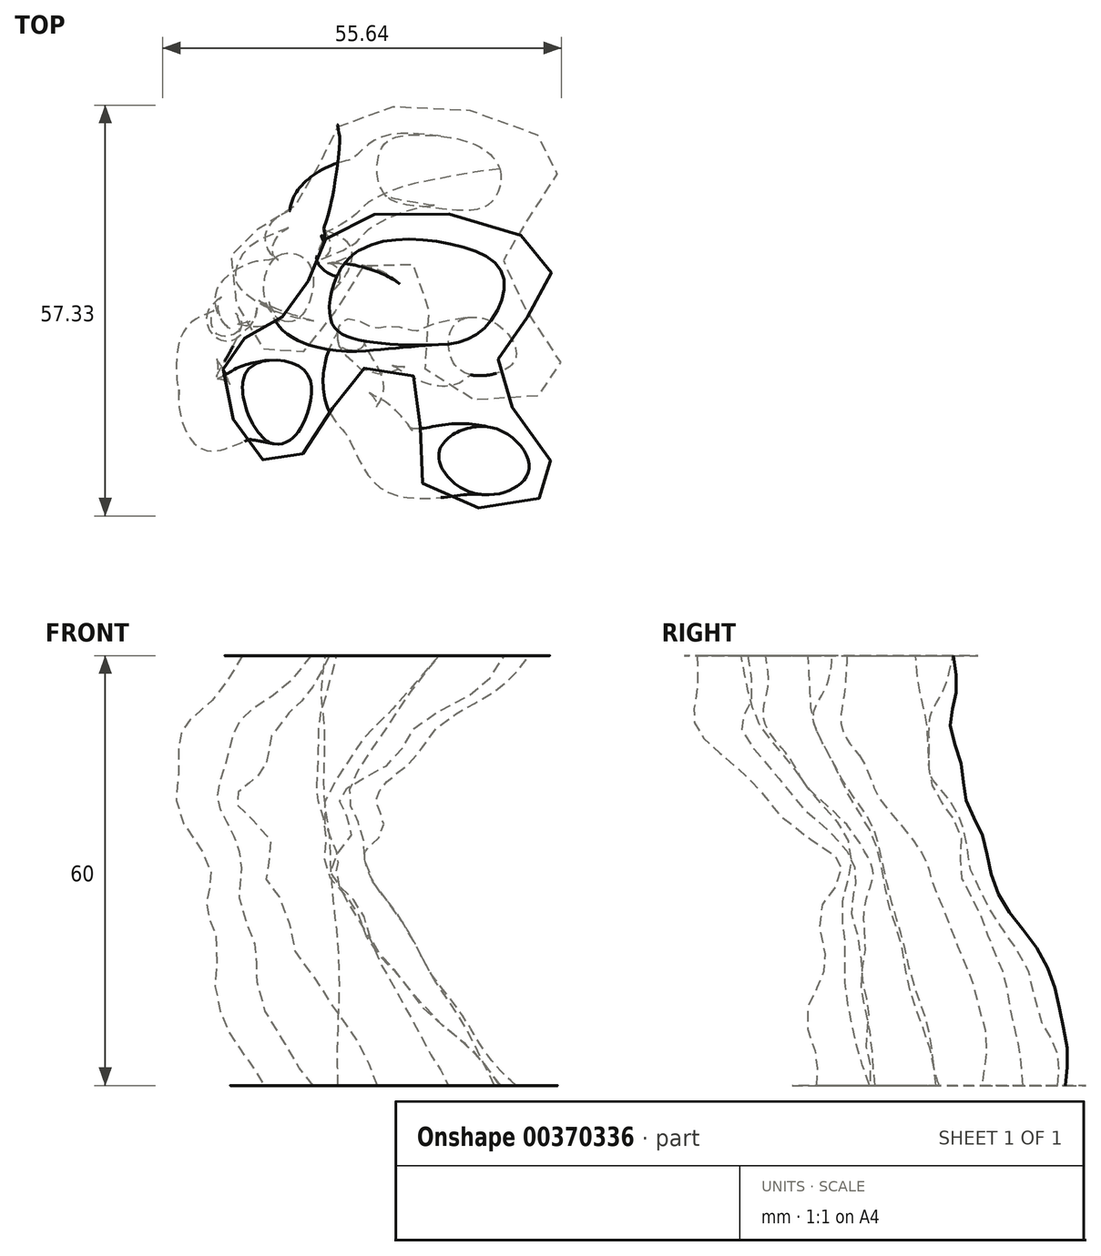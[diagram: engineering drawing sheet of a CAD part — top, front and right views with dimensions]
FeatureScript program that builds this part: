
annotation { "Feature Type Name" : "Feature", "Feature Type Description" : "" }
export const myFeature = defineFeature(function(context is Context, id is Id, definition is map)
    precondition{}
    {
        {
            var Q0;
            Q0=qCreatedBy(makeId("Top.planeOp"),FACE);
            cPlane(context, id + "F0", {"entities" : qUnion([Q0]), "cplaneType" : CPlaneType.OFFSET, "offset" : 5 * mm, "width" : 152.4 * mm, "height" : 152.4 * mm});
        }
        {
            var Q0;
            Q0=qCreatedBy(id+"F0.planeOp",FACE);
            var sketch = newSketch(context, id + "F1", { "sketchPlane" : qUnion([Q0])});
            skFitSpline(sketch, "E0", {"points": [v(-4.12, 24.5) * mm, v(12.71, 27.07) * mm, v(26.5, 20.1) * mm, v(22.26, 11.53) * mm, v(19.15, 3.69) * mm, v(26.98, -8.8) * mm, v(21.6, -13.7) * mm, v(8.13, -9.54) * mm, v(8.37, 3.2) * mm, v(0, 5.4) * mm, v(-6.08, -4.15) * mm, v(-12.69, -7.58) * mm, v(-18.32, 0) * mm, v(-18.32, 8.1) * mm, v(-12.69, 11.52) * mm, v(-7.54, 17.15) * mm, v(-4.12, 24.5) * mm]});
            skSolve(sketch);
        }
        {
            var Q0;
            Q0=qCreatedBy(id+"F0.planeOp",FACE);
            var sketch = newSketch(context, id + "F2", { "sketchPlane" : qUnion([Q0])});
            skFitSpline(sketch, "E1", {"points": [v(18.43, 18.57) * mm, v(16.76, 13.55) * mm, v(8.38, 13.27) * mm, v(2.23, 15.22) * mm, v(2.23, 21.92) * mm, v(8.1, 23.32) * mm, v(14.52, 22.2) * mm, v(18.43, 18.57) * mm]});
            skSolve(sketch);
        }
        {
            var Q0;
            Q0=qCreatedBy(id+"F0.planeOp",FACE);
            var sketch = newSketch(context, id + "F3", { "sketchPlane" : qUnion([Q0])});
            skFitSpline(sketch, "E2", {"points": [v(-12.55, 6.45) * mm, v(-8.36, 5.62) * mm, v(-8.08, 0.17) * mm, v(-10.88, -2.76) * mm, v(-14.23, 0.17) * mm, v(-12.55, 6.45) * mm]});
            skSolve(sketch);
        }
        {
            var Q0;
            Q0=qCreatedBy(id+"F0.planeOp",FACE);
            var sketch = newSketch(context, id + "F4", { "sketchPlane" : qUnion([Q0])});
            skFitSpline(sketch, "E3", {"points": [v(17.7, -2.86) * mm, v(20.7, -7.64) * mm, v(17.04, -10.13) * mm, v(12.22, -8.8) * mm, v(12.1, -3.14) * mm, v(17.7, -2.86) * mm]});
            skSolve(sketch);
        }
        {
            var Q0;
            Q0=qCreatedBy(id+"F0.planeOp",FACE);
            cPlane(context, id + "F5", {"entities" : qUnion([Q0]), "cplaneType" : CPlaneType.OFFSET, "offset" : 5 * mm, "width" : 152.4 * mm, "height" : 152.4 * mm});
        }
        {
            var Q0;
            Q0=qCreatedBy(id+"F5.planeOp",FACE);
            var sketch = newSketch(context, id + "F6", { "sketchPlane" : qUnion([Q0])});
            skFitSpline(sketch, "E4", {"points": [v(-7.05, 23.03) * mm, v(8.37, 25.24) * mm, v(21.1, 19.11) * mm, v(17.19, 11.52) * mm, v(14.74, 2.22) * mm, v(22.09, -9.05) * mm, v(17.19, -13.7) * mm, v(5.19, -10.27) * mm, v(5.43, 2.7) * mm, v(-3.38, 5.65) * mm, v(-10.48, -3.9) * mm, v(-16.85, -7.09) * mm, v(-20.77, 0) * mm, v(-20.28, 6.38) * mm, v(-14.9, 10.54) * mm, v(-10.48, 15.44) * mm, v(-7.05, 23.03) * mm]});
            skSolve(sketch);
        }
        {
            var Q0;
            Q0=qCreatedBy(id+"F5.planeOp",FACE);
            var sketch = newSketch(context, id + "F7", { "sketchPlane" : qUnion([Q0])});
            skFitSpline(sketch, "E5", {"points": [v(14.34, 18.87) * mm, v(13.14, 14.27) * mm, v(4.95, 14.07) * mm, v(0.15, 16.27) * mm, v(0, 21.86) * mm, v(7.15, 23.06) * mm, v(11.74, 21.66) * mm, v(14.34, 18.87) * mm]});
            skSolve(sketch);
        }
        {
            var Q0;
            Q0=qCreatedBy(id+"F5.planeOp",FACE);
            var sketch = newSketch(context, id + "F8", { "sketchPlane" : qUnion([Q0])});
            skFitSpline(sketch, "E6", {"points": [v(-16, 5.31) * mm, v(-11.56, 4.66) * mm, v(-12.52, -2) * mm, v(-15.68, -3.16) * mm, v(-17.67, 0) * mm, v(-16, 5.31) * mm]});
            skSolve(sketch);
        }
        {
            var Q0;
            Q0=qCreatedBy(id+"F5.planeOp",FACE);
            var sketch = newSketch(context, id + "F9", { "sketchPlane" : qUnion([Q0])});
            skFitSpline(sketch, "E7", {"points": [v(13.75, -3) * mm, v(16.15, -7.8) * mm, v(13.55, -10.39) * mm, v(9.07, -8.97) * mm, v(9.35, -3.6) * mm, v(13.75, -3) * mm]});
            skSolve(sketch);
        }
        {
            var Q0;
            Q0=qCreatedBy(id+"F5.planeOp",FACE);
            cPlane(context, id + "F10", {"entities" : qUnion([Q0]), "cplaneType" : CPlaneType.OFFSET, "offset" : 5 * mm, "width" : 152.4 * mm, "height" : 152.4 * mm});
        }
        {
            var Q0;
            Q0=qCreatedBy(id+"F10.planeOp",FACE);
            var sketch = newSketch(context, id + "F11", { "sketchPlane" : qUnion([Q0])});
            skFitSpline(sketch, "E8", {"points": [v(-8.03, 22.05) * mm, v(5.92, 23.28) * mm, v(15.47, 18.38) * mm, v(13.27, 11.03) * mm, v(11.56, 1) * mm, v(17.43, -8.8) * mm, v(13.02, -13.7) * mm, v(2.99, -10.76) * mm, v(3.47, 1.24) * mm, v(-4.85, 4.42) * mm, v(-12.2, -2.2) * mm, v(-17.83, -7.58) * mm, v(-21.5, -4.15) * mm, v(-22.73, 4.67) * mm, v(-17.58, 9.56) * mm, v(-12.2, 13.73) * mm, v(-8.03, 22.05) * mm]});
            skSolve(sketch);
        }
        {
            var Q0;
            Q0=qCreatedBy(id+"F10.planeOp",FACE);
            var sketch = newSketch(context, id + "F12", { "sketchPlane" : qUnion([Q0])});
            skFitSpline(sketch, "E9", {"points": [v(8.55, 15.27) * mm, v(6.55, 13.07) * mm, v(0, 13.07) * mm, v(-3.84, 15.47) * mm, v(-3.24, 19.27) * mm, v(2.75, 20.67) * mm, v(7.55, 19.07) * mm, v(8.55, 15.27) * mm]});
            skSolve(sketch);
        }
        {
            var Q0;
            Q0=qCreatedBy(id+"F10.planeOp",FACE);
            var sketch = newSketch(context, id + "F13", { "sketchPlane" : qUnion([Q0])});
            skFitSpline(sketch, "E10", {"points": [v(-19.66, 3.4) * mm, v(-15.66, 4.4) * mm, v(-14.46, -1) * mm, v(-18.17, -3) * mm, v(-20, -1.66) * mm, v(-19.66, 3.4) * mm]});
            skSolve(sketch);
        }
        {
            var Q0;
            Q0=qCreatedBy(id+"F10.planeOp",FACE);
            var sketch = newSketch(context, id + "F14", { "sketchPlane" : qUnion([Q0])});
            skFitSpline(sketch, "E11", {"points": [v(11.07, -3.7) * mm, v(13.06, -8.3) * mm, v(11.9, -11.3) * mm, v(6.9, -10.3) * mm, v(6.67, -4.5) * mm, v(11.07, -3.7) * mm]});
            skSolve(sketch);
        }
        {
            var Q0;
            Q0=qCreatedBy(id+"F10.planeOp",FACE);
            cPlane(context, id + "F15", {"entities" : qUnion([Q0]), "cplaneType" : CPlaneType.OFFSET, "offset" : 5 * mm, "width" : 152.4 * mm, "height" : 152.4 * mm});
        }
        {
            var Q0;
            Q0=qCreatedBy(id+"F15.planeOp",FACE);
            var sketch = newSketch(context, id + "F16", { "sketchPlane" : qUnion([Q0])});
            skFitSpline(sketch, "E12", {"points": [v(-9.5, 20.58) * mm, v(4.2, 21.8) * mm, v(12.05, 16.17) * mm, v(8.86, 9.07) * mm, v(8.37, 0) * mm, v(14.74, -6.35) * mm, v(7.88, -11.99) * mm, v(0, -8.56) * mm, v(1.52, 0) * mm, v(-6.08, 3.69) * mm, v(-10.97, 0) * mm, v(-13.91, -4.64) * mm, v(-20.03, -6.84) * mm, v(-22.73, 3.93) * mm, v(-17.34, 7.85) * mm, v(-13.42, 12.5) * mm, v(-9.5, 20.58) * mm]});
            skSolve(sketch);
        }
        {
            var Q0;
            Q0=qCreatedBy(id+"F15.planeOp",FACE);
            var sketch = newSketch(context, id + "F17", { "sketchPlane" : qUnion([Q0])});
            skFitSpline(sketch, "E13", {"points": [v(4.75, 15.47) * mm, v(2.75, 11.68) * mm, v(-3.44, 12.08) * mm, v(-7.04, 14.07) * mm, v(-6.64, 18.07) * mm, v(-1.6, 19.66) * mm, v(2.55, 18.87) * mm, v(4.75, 15.47) * mm]});
            skSolve(sketch);
        }
        {
            var Q0;
            Q0=qCreatedBy(id+"F15.planeOp",FACE);
            var sketch = newSketch(context, id + "F18", { "sketchPlane" : qUnion([Q0])});
            skFitSpline(sketch, "E14", {"points": [v(-20.9, 1.85) * mm, v(-16.93, 2.72) * mm, v(-15.5, -1.35) * mm, v(-17.3, -3.75) * mm, v(-20.1, -2.95) * mm, v(-20.9, 1.85) * mm]});
            skSolve(sketch);
        }
        {
            var Q0;
            Q0=qCreatedBy(id+"F15.planeOp",FACE);
            var sketch = newSketch(context, id + "F19", { "sketchPlane" : qUnion([Q0])});
            skFitSpline(sketch, "E15", {"points": [v(7.97, -4.39) * mm, v(9.17, -6.39) * mm, v(8.77, -8.58) * mm, v(3.78, -8.98) * mm, v(3.58, -4.99) * mm, v(7.97, -4.39) * mm]});
            skSolve(sketch);
        }
        {
            var Q0;
            Q0=qCreatedBy(id+"F15.planeOp",FACE);
            cPlane(context, id + "F20", {"entities" : qUnion([Q0]), "cplaneType" : CPlaneType.OFFSET, "offset" : 5 * mm, "width" : 152.4 * mm, "height" : 152.4 * mm});
        }
        {
            var Q0;
            Q0=qCreatedBy(id+"F20.planeOp",FACE);
            var sketch = newSketch(context, id + "F21", { "sketchPlane" : qUnion([Q0])});
            skFitSpline(sketch, "E16", {"points": [v(-13.18, 17.64) * mm, v(0, 19.11) * mm, v(6.66, 13.48) * mm, v(3.47, 8.58) * mm, v(4.2, 0) * mm, v(10.09, -5.37) * mm, v(7.64, -10.03) * mm, v(0, -10.76) * mm, v(-2.4, -1.95) * mm, v(-8.03, 0) * mm, v(-12.69, -1.95) * mm, v(-14.4, -5.86) * mm, v(-17.83, -8.31) * mm, v(-22.24, -3.41) * mm, v(-21.5, 4.18) * mm, v(-15.87, 9.8) * mm, v(-13.18, 17.64) * mm]});
            skSolve(sketch);
        }
        {
            var Q0;
            Q0=qCreatedBy(id+"F20.planeOp",FACE);
            var sketch = newSketch(context, id + "F22", { "sketchPlane" : qUnion([Q0])});
            skFitSpline(sketch, "E17", {"points": [v(0, 14.47) * mm, v(0, 10.08) * mm, v(-5.44, 9.48) * mm, v(-10.03, 11.48) * mm, v(-10.23, 14.87) * mm, v(-6.84, 16.87) * mm, v(-3.44, 16.67) * mm, v(0, 14.47) * mm]});
            skSolve(sketch);
        }
        {
            var Q0;
            Q0=qCreatedBy(id+"F20.planeOp",FACE);
            var sketch = newSketch(context, id + "F23", { "sketchPlane" : qUnion([Q0])});
            skFitSpline(sketch, "E18", {"points": [v(-20.77, 0.14) * mm, v(-17.77, 1.83) * mm, v(-15.78, -1.37) * mm, v(-17.57, -4.17) * mm, v(-19.77, -3.57) * mm, v(-20.77, 0.14) * mm]});
            skSolve(sketch);
        }
        {
            var Q0;
            Q0=qCreatedBy(id+"F20.planeOp",FACE);
            var sketch = newSketch(context, id + "F24", { "sketchPlane" : qUnion([Q0])});
            skFitSpline(sketch, "E19", {"points": [v(4.46, -3.62) * mm, v(6.46, -5.62) * mm, v(5.08, -8.97) * mm, v(1.46, -8.41) * mm, v(1.07, -4.22) * mm, v(4.46, -3.62) * mm]});
            skSolve(sketch);
        }
        {
            var Q0;
            Q0=qCreatedBy(id+"F20.planeOp",FACE);
            cPlane(context, id + "F25", {"entities" : qUnion([Q0]), "cplaneType" : CPlaneType.OFFSET, "offset" : 5 * mm, "width" : 152.4 * mm, "height" : 152.4 * mm});
        }
        {
            var Q0;
            Q0=qCreatedBy(id+"F25.planeOp",FACE);
            var sketch = newSketch(context, id + "F26", { "sketchPlane" : qUnion([Q0])});
            skFitSpline(sketch, "E20", {"points": [v(-12.82, 14.5) * mm, v(-2.24, 15.58) * mm, v(3.73, 10.96) * mm, v(0, 5.8) * mm, v(0, 0) * mm, v(6.45, -5.86) * mm, v(4.82, -10.74) * mm, v(-2.5, -11.29) * mm, v(-5.5, -3.15) * mm, v(-10.65, 0) * mm, v(-15.53, -3.15) * mm, v(-15.8, -6.4) * mm, v(-20.14, -8.03) * mm, v(-25.57, 0) * mm, v(-23.13, 2.82) * mm, v(-15.3, 8.02) * mm, v(-12.82, 14.5) * mm]});
            skSolve(sketch);
        }
        {
            var Q0;
            Q0=qCreatedBy(id+"F25.planeOp",FACE);
            var sketch = newSketch(context, id + "F27", { "sketchPlane" : qUnion([Q0])});
            skFitSpline(sketch, "E21", {"points": [v(-1.64, 11.88) * mm, v(-2.04, 8.08) * mm, v(-7.44, 7.68) * mm, v(-11.03, 9.48) * mm, v(-11.03, 12.67) * mm, v(-8.04, 13.67) * mm, v(-4.64, 13.07) * mm, v(-1.64, 11.88) * mm]});
            skSolve(sketch);
        }
        {
            var Q0;
            Q0=qCreatedBy(id+"F25.planeOp",FACE);
            var sketch = newSketch(context, id + "F28", { "sketchPlane" : qUnion([Q0])});
            skFitSpline(sketch, "E22", {"points": [v(-22.4, -1.58) * mm, v(-19.8, 0.41) * mm, v(-18, -1.78) * mm, v(-18.33, -4.99) * mm, v(-21, -4.99) * mm, v(-22.4, -1.58) * mm]});
            skSolve(sketch);
        }
        {
            var Q0;
            Q0=qCreatedBy(id+"F25.planeOp",FACE);
            var sketch = newSketch(context, id + "F29", { "sketchPlane" : qUnion([Q0])});
            skFitSpline(sketch, "E23", {"points": [v(1.34, -3.72) * mm, v(3.34, -6.92) * mm, v(2.34, -9.12) * mm, v(-1.44, -8.98) * mm, v(-2.06, -4.92) * mm, v(1.34, -3.72) * mm]});
            skSolve(sketch);
        }
        {
            var Q0;
            Q0=qCreatedBy(id+"F25.planeOp",FACE);
            cPlane(context, id + "F30", {"entities" : qUnion([Q0]), "cplaneType" : CPlaneType.OFFSET, "offset" : 5 * mm, "width" : 152.4 * mm, "height" : 152.4 * mm});
        }
        {
            var Q0;
            Q0=qCreatedBy(id+"F30.planeOp",FACE);
            var sketch = newSketch(context, id + "F31", { "sketchPlane" : qUnion([Q0])});
            skFitSpline(sketch, "E24", {"points": [v(-15.83, 12.08) * mm, v(-5.64, 14.07) * mm, v(0, 10.48) * mm, v(-2.24, 4.68) * mm, v(-1.84, 0) * mm, v(2.95, -4.5) * mm, v(2.35, -7.1) * mm, v(-5.44, -8.1) * mm, v(-6.84, 0) * mm, v(-11.23, 1.69) * mm, v(-15.23, -1.9) * mm, v(-15.83, -6.3) * mm, v(-20.62, -7.5) * mm, v(-23.82, -2.3) * mm, v(-23.02, 2.29) * mm, v(-18.02, 7.28) * mm, v(-15.83, 12.08) * mm]});
            skSolve(sketch);
        }
        {
            var Q0;
            Q0=qCreatedBy(id+"F30.planeOp",FACE);
            var sketch = newSketch(context, id + "F32", { "sketchPlane" : qUnion([Q0])});
            skFitSpline(sketch, "E25", {"points": [v(-6.24, 10.48) * mm, v(-5.44, 6.88) * mm, v(-9.83, 5.48) * mm, v(-13.43, 6.68) * mm, v(-14.23, 9.08) * mm, v(-12.63, 10.88) * mm, v(-8.84, 11.28) * mm, v(-6.24, 10.48) * mm]});
            skSolve(sketch);
        }
        {
            var Q0;
            Q0=qCreatedBy(id+"F30.planeOp",FACE);
            var sketch = newSketch(context, id + "F33", { "sketchPlane" : qUnion([Q0])});
            skFitSpline(sketch, "E26", {"points": [v(-21.53, -1.24) * mm, v(-18.93, -1.24) * mm, v(-17.53, -3.03) * mm, v(-18.53, -4.43) * mm, v(-21.13, -4.43) * mm, v(-21.53, -1.24) * mm]});
            skSolve(sketch);
        }
        {
            var Q0;
            Q0=qCreatedBy(id+"F30.planeOp",FACE);
            var sketch = newSketch(context, id + "F34", { "sketchPlane" : qUnion([Q0])});
            skFitSpline(sketch, "E27", {"points": [v(-2.64, -2.35) * mm, v(0, -4.55) * mm, v(-1.04, -6.55) * mm, v(-3.84, -6.15) * mm, v(-4.24, -3.95) * mm, v(-2.64, -2.35) * mm]});
            skSolve(sketch);
        }
        {
            var Q0;
            Q0=qCreatedBy(id+"F30.planeOp",FACE);
            cPlane(context, id + "F35", {"entities" : qUnion([Q0]), "cplaneType" : CPlaneType.OFFSET, "offset" : 5 * mm, "width" : 152.4 * mm, "height" : 152.4 * mm});
        }
        {
            var Q0;
            Q0=qCreatedBy(id+"F35.planeOp",FACE);
            var sketch = newSketch(context, id + "F36", { "sketchPlane" : qUnion([Q0])});
            skFitSpline(sketch, "E28", {"points": [v(-14.78, 11.48) * mm, v(-4.2, 12.57) * mm, v(1.77, 7.96) * mm, v(-1.97, 2.8) * mm, v(-1.97, -3) * mm, v(4.48, -8.87) * mm, v(2.85, -13.75) * mm, v(-4.47, -14.3) * mm, v(-7.46, -6.15) * mm, v(-12.61, -3) * mm, v(-17.5, -6.15) * mm, v(-17.77, -9.4) * mm, v(-22.11, -11.04) * mm, v(-27.54, -3) * mm, v(-25.1, -0.18) * mm, v(-17.27, 5.01) * mm, v(-14.78, 11.48) * mm]});
            skSolve(sketch);
        }
        {
            var Q0;
            Q0=qCreatedBy(id+"F35.planeOp",FACE);
            var sketch = newSketch(context, id + "F37", { "sketchPlane" : qUnion([Q0])});
            skFitSpline(sketch, "E29", {"points": [v(-2.27, 7.4) * mm, v(-4.04, 3.54) * mm, v(-9.01, 2.74) * mm, v(-12.86, 4.02) * mm, v(-13.98, 6.75) * mm, v(-12.06, 9.96) * mm, v(-5.48, 9.8) * mm, v(-2.27, 7.4) * mm]});
            skSolve(sketch);
        }
        {
            var Q0;
            Q0=qCreatedBy(id+"F35.planeOp",FACE);
            var sketch = newSketch(context, id + "F38", { "sketchPlane" : qUnion([Q0])});
            skFitSpline(sketch, "E30", {"points": [v(-24.32, -2.67) * mm, v(-19.66, -2.67) * mm, v(-18.7, -4.92) * mm, v(-19.57, -7.32) * mm, v(-23.03, -7.32) * mm, v(-24.32, -2.67) * mm]});
            skSolve(sketch);
        }
        {
            var Q0;
            Q0=qCreatedBy(id+"F35.planeOp",FACE);
            var sketch = newSketch(context, id + "F39", { "sketchPlane" : qUnion([Q0])});
            skFitSpline(sketch, "E31", {"points": [v(-2.5, -4.98) * mm, v(0.23, -7.25) * mm, v(1.7, -11.1) * mm, v(-3.03, -11.45) * mm, v(-5.13, -6.03) * mm, v(-2.5, -4.98) * mm]});
            skSolve(sketch);
        }
        {
            var Q0;
            Q0=qCreatedBy(id+"F35.planeOp",FACE);
            cPlane(context, id + "F40", {"entities" : qUnion([Q0]), "cplaneType" : CPlaneType.OFFSET, "offset" : 5 * mm, "width" : 152.4 * mm, "height" : 152.4 * mm});
        }
        {
            var Q0;
            Q0=qCreatedBy(id+"F40.planeOp",FACE);
            var sketch = newSketch(context, id + "F41", { "sketchPlane" : qUnion([Q0])});
            skFitSpline(sketch, "E32", {"points": [v(-18.89, 9) * mm, v(-5.71, 10.47) * mm, v(0.94, 4.84) * mm, v(-2.24, -0.06) * mm, v(-1.5, -8.65) * mm, v(4.37, -14.02) * mm, v(1.92, -18.67) * mm, v(-5.71, -19.4) * mm, v(-8.12, -10.6) * mm, v(-13.75, -8.65) * mm, v(-18.4, -10.6) * mm, v(-20.11, -14.5) * mm, v(-23.54, -16.96) * mm, v(-27.95, -12.06) * mm, v(-27.22, -4.47) * mm, v(-21.58, 1.16) * mm, v(-18.89, 9) * mm]});
            skSolve(sketch);
        }
        {
            var Q0;
            Q0=qCreatedBy(id+"F40.planeOp",FACE);
            var sketch = newSketch(context, id + "F42", { "sketchPlane" : qUnion([Q0])});
            skFitSpline(sketch, "E33", {"points": [v(-3.97, 4.35) * mm, v(-5.9, 0) * mm, v(-11.84, -1.25) * mm, v(-17.44, 1.72) * mm, v(-18.49, 3.82) * mm, v(-16.39, 7.5) * mm, v(-8.69, 7.5) * mm, v(-3.97, 4.35) * mm]});
            skSolve(sketch);
        }
        {
            var Q0;
            Q0=qCreatedBy(id+"F40.planeOp",FACE);
            var sketch = newSketch(context, id + "F43", { "sketchPlane" : qUnion([Q0])});
            skFitSpline(sketch, "E34", {"points": [v(-25.83, -5.62) * mm, v(-21.98, -5.62) * mm, v(-20.93, -9.47) * mm, v(-22.33, -12.8) * mm, v(-25.48, -12.8) * mm, v(-25.83, -5.62) * mm]});
            skSolve(sketch);
        }
        {
            var Q0;
            Q0=qCreatedBy(id+"F40.planeOp",FACE);
            var sketch = newSketch(context, id + "F44", { "sketchPlane" : qUnion([Q0])});
            skFitSpline(sketch, "E35", {"points": [v(-3.1, -10) * mm, v(1.28, -14.54) * mm, v(-2.4, -17.17) * mm, v(-5.37, -15.24) * mm, v(-5.37, -10.7) * mm, v(-3.1, -10) * mm]});
            skSolve(sketch);
        }
        {
            var Q0;
            Q0=qCreatedBy(id+"F40.planeOp",FACE);
            cPlane(context, id + "F45", {"entities" : qUnion([Q0]), "cplaneType" : CPlaneType.OFFSET, "offset" : 5 * mm, "width" : 152.4 * mm, "height" : 152.4 * mm});
        }
        {
            var Q0;
            Q0=qCreatedBy(id+"F45.planeOp",FACE);
            var sketch = newSketch(context, id + "F46", { "sketchPlane" : qUnion([Q0])});
            skFitSpline(sketch, "E36", {"points": [v(-14.52, 7.84) * mm, v(-0.8, 9.06) * mm, v(7.03, 3.43) * mm, v(3.84, -3.67) * mm, v(3.35, -12.75) * mm, v(9.72, -19.1) * mm, v(2.86, -24.73) * mm, v(-5.02, -21.3) * mm, v(-3.5, -12.75) * mm, v(-11.1, -9.06) * mm, v(-16, -12.75) * mm, v(-18.93, -17.38) * mm, v(-25.05, -19.59) * mm, v(-27.74, -8.81) * mm, v(-22.36, -4.9) * mm, v(-18.44, -0.24) * mm, v(-14.52, 7.84) * mm]});
            skSolve(sketch);
        }
        {
            var Q0;
            Q0=qCreatedBy(id+"F45.planeOp",FACE);
            var sketch = newSketch(context, id + "F47", { "sketchPlane" : qUnion([Q0])});
            skFitSpline(sketch, "E37", {"points": [v(3.03, 2.6) * mm, v(0, -2.82) * mm, v(-6.77, -3.35) * mm, v(-12.01, -2.3) * mm, v(-14.11, 1.55) * mm, v(-12.19, 4.17) * mm, v(-3.1, 5.4) * mm, v(3.03, 2.6) * mm]});
            skSolve(sketch);
        }
        {
            var Q0;
            Q0=qCreatedBy(id+"F45.planeOp",FACE);
            var sketch = newSketch(context, id + "F48", { "sketchPlane" : qUnion([Q0])});
            skFitSpline(sketch, "E38", {"points": [v(-25.13, -8.77) * mm, v(-20.58, -8.77) * mm, v(-19.88, -13.32) * mm, v(-21.28, -16.47) * mm, v(-25.13, -16.47) * mm, v(-25.13, -8.77) * mm]});
            skSolve(sketch);
        }
        {
            var Q0;
            Q0=qCreatedBy(id+"F45.planeOp",FACE);
            var sketch = newSketch(context, id + "F49", { "sketchPlane" : qUnion([Q0])});
            skFitSpline(sketch, "E39", {"points": [v(1.8, -13.67) * mm, v(5.83, -19.8) * mm, v(2.16, -22.07) * mm, v(-1.87, -20.32) * mm, v(-2.57, -15.94) * mm, v(1.8, -13.67) * mm]});
            skSolve(sketch);
        }
        {
            var Q0;
            Q0=qCreatedBy(id+"F45.planeOp",FACE);
            cPlane(context, id + "F50", {"entities" : qUnion([Q0]), "cplaneType" : CPlaneType.OFFSET, "offset" : 5 * mm, "width" : 152.4 * mm, "height" : 152.4 * mm});
        }
        {
            var Q0;
            Q0=qCreatedBy(id+"F50.planeOp",FACE);
            var sketch = newSketch(context, id + "F51", { "sketchPlane" : qUnion([Q0])});
            skFitSpline(sketch, "E40", {"points": [v(-12.26, 6.45) * mm, v(1.7, 7.68) * mm, v(11.25, 2.78) * mm, v(9.05, -4.57) * mm, v(7.33, -14.6) * mm, v(13.2, -24.4) * mm, v(8.8, -29.3) * mm, v(-1.24, -26.36) * mm, v(-0.75, -14.36) * mm, v(-9.07, -11.18) * mm, v(-16.42, -17.8) * mm, v(-22.05, -23.18) * mm, v(-25.73, -19.75) * mm, v(-26.95, -10.93) * mm, v(-21.8, -6.04) * mm, v(-16.42, -1.87) * mm, v(-12.26, 6.45) * mm]});
            skSolve(sketch);
        }
        {
            var Q0;
            Q0=qCreatedBy(id+"F50.planeOp",FACE);
            var sketch = newSketch(context, id + "F52", { "sketchPlane" : qUnion([Q0])});
            skFitSpline(sketch, "E41", {"points": [v(6.58, 0) * mm, v(4.42, -3.99) * mm, v(-2.06, -6.65) * mm, v(-10.03, -5.15) * mm, v(-12.85, -1.17) * mm, v(-8.54, 4.65) * mm, v(1.76, 4.15) * mm, v(6.58, 0) * mm]});
            skSolve(sketch);
        }
        {
            var Q0;
            Q0=qCreatedBy(id+"F50.planeOp",FACE);
            var sketch = newSketch(context, id + "F53", { "sketchPlane" : qUnion([Q0])});
            skFitSpline(sketch, "E42", {"points": [v(-24.98, -11.63) * mm, v(-19, -11.63) * mm, v(-19.16, -17.77) * mm, v(-20.5, -20.26) * mm, v(-23.15, -20.26) * mm, v(-24.98, -11.63) * mm]});
            skSolve(sketch);
        }
        {
            var Q0;
            Q0=qCreatedBy(id+"F50.planeOp",FACE);
            var sketch = newSketch(context, id + "F54", { "sketchPlane" : qUnion([Q0])});
            skFitSpline(sketch, "E43", {"points": [v(5.25, -17.27) * mm, v(9.73, -23.75) * mm, v(7.29, -26.68) * mm, v(2.26, -26.08) * mm, v(1.26, -20.1) * mm, v(5.25, -17.27) * mm]});
            skSolve(sketch);
        }
        {
            var Q0;
            Q0=qCreatedBy(id+"F50.planeOp",FACE);
            cPlane(context, id + "F55", {"entities" : qUnion([Q0]), "cplaneType" : CPlaneType.OFFSET, "offset" : 5 * mm, "width" : 152.4 * mm, "height" : 152.4 * mm});
        }
        {
            var Q0;
            Q0=qCreatedBy(id+"F55.planeOp",FACE);
            var sketch = newSketch(context, id + "F56", { "sketchPlane" : qUnion([Q0])});
            skFitSpline(sketch, "E44", {"points": [v(-7.93, 8.21) * mm, v(7.5, 10.41) * mm, v(20.23, 4.3) * mm, v(16.31, -3.3) * mm, v(13.86, -12.6) * mm, v(21.2, -23.87) * mm, v(16.31, -28.52) * mm, v(4.31, -25.1) * mm, v(4.56, -12.11) * mm, v(-4.26, -9.18) * mm, v(-11.36, -18.73) * mm, v(-17.73, -21.9) * mm, v(-21.64, -14.82) * mm, v(-21.15, -8.44) * mm, v(-15.77, -4.28) * mm, v(-11.36, 0.62) * mm, v(-7.93, 8.21) * mm]});
            skSolve(sketch);
        }
        {
            var Q0;
            Q0=qCreatedBy(id+"F55.planeOp",FACE);
            var sketch = newSketch(context, id + "F57", { "sketchPlane" : qUnion([Q0])});
            skFitSpline(sketch, "E45", {"points": [v(15.05, 1.66) * mm, v(11.72, -3) * mm, v(6.08, -6.15) * mm, v(-3.47, -5.14) * mm, v(-8.04, -2) * mm, v(-3.72, 5.8) * mm, v(8.4, 6.3) * mm, v(15.05, 1.66) * mm]});
            skSolve(sketch);
        }
        {
            var Q0;
            Q0=qCreatedBy(id+"F55.planeOp",FACE);
            var sketch = newSketch(context, id + "F58", { "sketchPlane" : qUnion([Q0])});
            skFitSpline(sketch, "E46", {"points": [v(-20, -10.47) * mm, v(-13.68, -10.47) * mm, v(-12.85, -16.44) * mm, v(-14.68, -18.6) * mm, v(-18.17, -18.6) * mm, v(-20, -10.47) * mm]});
            skSolve(sketch);
        }
        {
            var Q0;
            Q0=qCreatedBy(id+"F55.planeOp",FACE);
            var sketch = newSketch(context, id + "F59", { "sketchPlane" : qUnion([Q0])});
            skFitSpline(sketch, "E47", {"points": [v(12.5, -17.31) * mm, v(17.7, -23.92) * mm, v(14.53, -26.72) * mm, v(7.9, -25.41) * mm, v(5.91, -20.1) * mm, v(12.5, -17.31) * mm]});
            skSolve(sketch);
        }
        {
            var Q0;
            Q0=qCreatedBy(id+"F55.planeOp",FACE);
            cPlane(context, id + "F60", {"entities" : qUnion([Q0]), "cplaneType" : CPlaneType.OFFSET, "offset" : 5 * mm, "width" : 152.4 * mm, "height" : 152.4 * mm});
        }
        {
            var Q0;
            Q0=qCreatedBy(id+"F60.planeOp",FACE);
            var sketch = newSketch(context, id + "F61", { "sketchPlane" : qUnion([Q0])});
            skFitSpline(sketch, "E48", {"points": [v(-5.1, 9.67) * mm, v(11.73, 12.24) * mm, v(25.52, 5.26) * mm, v(21.28, -3.3) * mm, v(18.17, -11.14) * mm, v(26, -23.63) * mm, v(20.62, -28.53) * mm, v(7.15, -24.37) * mm, v(7.4, -11.63) * mm, v(-0.98, -9.43) * mm, v(-7.05, -18.98) * mm, v(-13.66, -22.4) * mm, v(-19.3, -14.83) * mm, v(-19.3, -6.74) * mm, v(-13.66, -3.3) * mm, v(-8.52, 2.33) * mm, v(-5.1, 9.67) * mm]});
            skSolve(sketch);
        }
        {
            var Q0;
            Q0=qCreatedBy(id+"F60.planeOp",FACE);
            var sketch = newSketch(context, id + "F62", { "sketchPlane" : qUnion([Q0])});
            skFitSpline(sketch, "E49", {"points": [v(18.87, 3.82) * mm, v(15.88, -3.99) * mm, v(8.24, -5.98) * mm, v(-2.22, -4.99) * mm, v(-5.21, -2.16) * mm, v(-2.4, 6.3) * mm, v(9.73, 8.47) * mm, v(18.87, 3.82) * mm]});
            skSolve(sketch);
        }
        {
            var Q0;
            Q0=qCreatedBy(id+"F60.planeOp",FACE);
            var sketch = newSketch(context, id + "F63", { "sketchPlane" : qUnion([Q0])});
            skFitSpline(sketch, "E50", {"points": [v(-16.84, -9.64) * mm, v(-8.7, -9.64) * mm, v(-8.87, -16.61) * mm, v(-10.86, -19.27) * mm, v(-14.18, -19.27) * mm, v(-16.84, -9.64) * mm]});
            skSolve(sketch);
        }
        {
            var Q0;
            Q0=qCreatedBy(id+"F60.planeOp",FACE);
            var sketch = newSketch(context, id + "F64", { "sketchPlane" : qUnion([Q0])});
            skFitSpline(sketch, "E51", {"points": [v(17.04, -17.44) * mm, v(22.52, -22.59) * mm, v(19.86, -26.24) * mm, v(13.05, -25.9) * mm, v(10.06, -20.6) * mm, v(17.04, -17.44) * mm]});
            skSolve(sketch);
        }
        {
            var Q0;
            Q0 = qSketchRegion(id + "F2", true);
            var Q1;
            Q1 = qSketchRegion(id + "F7", true);
            var Q2;
            Q2 = qSketchRegion(id + "F12", true);
            var Q3;
            Q3 = qSketchRegion(id + "F17", true);
            var Q4;
            Q4 = qSketchRegion(id + "F22", true);
            var Q5;
            Q5 = qSketchRegion(id + "F27", true);
            var Q6;
            Q6 = qSketchRegion(id + "F32", true);
            var Q7;
            Q7 = qSketchRegion(id + "F37", true);
            var Q8;
            Q8 = qSketchRegion(id + "F42", true);
            var Q9;
            Q9 = qSketchRegion(id + "F47", true);
            var Q10;
            Q10 = qSketchRegion(id + "F52", true);
            var Q11;
            Q11 = qSketchRegion(id + "F57", true);
            var Q12;
            Q12 = qSketchRegion(id + "F62", true);
            loft(context, id + "F65", {"sheetProfilesArray" : [{ "sheetProfileEntities" : qUnion([Q0]) }, { "sheetProfileEntities" : qUnion([Q1]) }, { "sheetProfileEntities" : qUnion([Q2]) }, { "sheetProfileEntities" : qUnion([Q3]) }, { "sheetProfileEntities" : qUnion([Q4]) }, { "sheetProfileEntities" : qUnion([Q5]) }, { "sheetProfileEntities" : qUnion([Q6]) }, { "sheetProfileEntities" : qUnion([Q7]) }, { "sheetProfileEntities" : qUnion([Q8]) }, { "sheetProfileEntities" : qUnion([Q9]) }, { "sheetProfileEntities" : qUnion([Q10]) }, { "sheetProfileEntities" : qUnion([Q11]) }, { "sheetProfileEntities" : qUnion([Q12]) }]});
        }
        {
            var Q0;
            Q0 = qSketchRegion(id + "F3", true);
            var Q1;
            Q1 = qSketchRegion(id + "F8", true);
            var Q2;
            Q2 = qSketchRegion(id + "F13", true);
            var Q3;
            Q3 = qSketchRegion(id + "F18", true);
            var Q4;
            Q4 = qSketchRegion(id + "F23", true);
            var Q5;
            Q5 = qSketchRegion(id + "F28", true);
            var Q6;
            Q6 = qSketchRegion(id + "F33", true);
            var Q7;
            Q7 = qSketchRegion(id + "F38", true);
            var Q8;
            Q8 = qSketchRegion(id + "F43", true);
            var Q9;
            Q9 = qSketchRegion(id + "F48", true);
            var Q10;
            Q10 = qSketchRegion(id + "F53", true);
            var Q11;
            Q11 = qSketchRegion(id + "F58", true);
            var Q12;
            Q12 = qSketchRegion(id + "F63", true);
            loft(context, id + "F66", {"sheetProfilesArray" : [{ "sheetProfileEntities" : qUnion([Q0]) }, { "sheetProfileEntities" : qUnion([Q1]) }, { "sheetProfileEntities" : qUnion([Q2]) }, { "sheetProfileEntities" : qUnion([Q3]) }, { "sheetProfileEntities" : qUnion([Q4]) }, { "sheetProfileEntities" : qUnion([Q5]) }, { "sheetProfileEntities" : qUnion([Q6]) }, { "sheetProfileEntities" : qUnion([Q7]) }, { "sheetProfileEntities" : qUnion([Q8]) }, { "sheetProfileEntities" : qUnion([Q9]) }, { "sheetProfileEntities" : qUnion([Q10]) }, { "sheetProfileEntities" : qUnion([Q11]) }, { "sheetProfileEntities" : qUnion([Q12]) }]});
        }
        {
            var Q0;
            Q0 = qSketchRegion(id + "F4", true);
            var Q1;
            Q1 = qSketchRegion(id + "F9", true);
            var Q2;
            Q2 = qSketchRegion(id + "F14", true);
            var Q3;
            Q3 = qSketchRegion(id + "F19", true);
            var Q4;
            Q4 = qSketchRegion(id + "F24", true);
            var Q5;
            Q5 = qSketchRegion(id + "F29", true);
            var Q6;
            Q6 = qSketchRegion(id + "F34", true);
            var Q7;
            Q7 = qSketchRegion(id + "F39", true);
            var Q8;
            Q8 = qSketchRegion(id + "F44", true);
            var Q9;
            Q9 = qSketchRegion(id + "F49", true);
            var Q10;
            Q10 = qSketchRegion(id + "F54", true);
            var Q11;
            Q11 = qSketchRegion(id + "F59", true);
            var Q12;
            Q12 = qSketchRegion(id + "F64", true);
            loft(context, id + "F67", {"sheetProfilesArray" : [{ "sheetProfileEntities" : qUnion([Q0]) }, { "sheetProfileEntities" : qUnion([Q1]) }, { "sheetProfileEntities" : qUnion([Q2]) }, { "sheetProfileEntities" : qUnion([Q3]) }, { "sheetProfileEntities" : qUnion([Q4]) }, { "sheetProfileEntities" : qUnion([Q5]) }, { "sheetProfileEntities" : qUnion([Q6]) }, { "sheetProfileEntities" : qUnion([Q7]) }, { "sheetProfileEntities" : qUnion([Q8]) }, { "sheetProfileEntities" : qUnion([Q9]) }, { "sheetProfileEntities" : qUnion([Q10]) }, { "sheetProfileEntities" : qUnion([Q11]) }, { "sheetProfileEntities" : qUnion([Q12]) }]});
        }
        {
            var Q0;
            Q0 = qSketchRegion(id + "F1", true);
            var Q1;
            Q1 = qSketchRegion(id + "F6", true);
            var Q2;
            Q2 = qSketchRegion(id + "F11", true);
            var Q3;
            Q3 = qSketchRegion(id + "F16", true);
            var Q4;
            Q4 = qSketchRegion(id + "F21", true);
            var Q5;
            Q5 = qSketchRegion(id + "F26", true);
            var Q6;
            Q6 = qSketchRegion(id + "F31", true);
            var Q7;
            Q7 = qSketchRegion(id + "F36", true);
            var Q8;
            Q8 = qSketchRegion(id + "F41", true);
            var Q9;
            Q9 = qSketchRegion(id + "F46", true);
            var Q10;
            Q10 = qSketchRegion(id + "F51", true);
            var Q11;
            Q11 = qSketchRegion(id + "F56", true);
            var Q12;
            Q12 = qSketchRegion(id + "F61", true);
            loft(context, id + "F68", {"sheetProfilesArray" : [{ "sheetProfileEntities" : qUnion([Q0]) }, { "sheetProfileEntities" : qUnion([Q1]) }, { "sheetProfileEntities" : qUnion([Q2]) }, { "sheetProfileEntities" : qUnion([Q3]) }, { "sheetProfileEntities" : qUnion([Q4]) }, { "sheetProfileEntities" : qUnion([Q5]) }, { "sheetProfileEntities" : qUnion([Q6]) }, { "sheetProfileEntities" : qUnion([Q7]) }, { "sheetProfileEntities" : qUnion([Q8]) }, { "sheetProfileEntities" : qUnion([Q9]) }, { "sheetProfileEntities" : qUnion([Q10]) }, { "sheetProfileEntities" : qUnion([Q11]) }, { "sheetProfileEntities" : qUnion([Q12]) }]});
        }
        {
            var Q0;
            Q0 = qSketchRegion(id + "F2", true);
            var Q1;
            Q1 = qSketchRegion(id + "F7", true);
            var Q2;
            Q2 = qSketchRegion(id + "F12", true);
            var Q3;
            Q3 = qSketchRegion(id + "F17", true);
            var Q4;
            Q4 = qSketchRegion(id + "F22", true);
            var Q5;
            Q5 = qSketchRegion(id + "F27", true);
            var Q6;
            Q6 = qSketchRegion(id + "F32", true);
            var Q7;
            Q7 = qSketchRegion(id + "F37", true);
            var Q8;
            Q8 = qSketchRegion(id + "F42", true);
            var Q9;
            Q9 = qSketchRegion(id + "F47", true);
            var Q10;
            Q10 = qSketchRegion(id + "F52", true);
            var Q11;
            Q11 = qSketchRegion(id + "F57", true);
            var Q12;
            Q12 = qSketchRegion(id + "F62", true);
            loft(context, id + "F69", {"operationType" : NewBodyOperationType.REMOVE, "sheetProfilesArray" : [{ "sheetProfileEntities" : qUnion([Q0]) }, { "sheetProfileEntities" : qUnion([Q1]) }, { "sheetProfileEntities" : qUnion([Q2]) }, { "sheetProfileEntities" : qUnion([Q3]) }, { "sheetProfileEntities" : qUnion([Q4]) }, { "sheetProfileEntities" : qUnion([Q5]) }, { "sheetProfileEntities" : qUnion([Q6]) }, { "sheetProfileEntities" : qUnion([Q7]) }, { "sheetProfileEntities" : qUnion([Q8]) }, { "sheetProfileEntities" : qUnion([Q9]) }, { "sheetProfileEntities" : qUnion([Q10]) }, { "sheetProfileEntities" : qUnion([Q11]) }, { "sheetProfileEntities" : qUnion([Q12]) }]});
        }
    });
